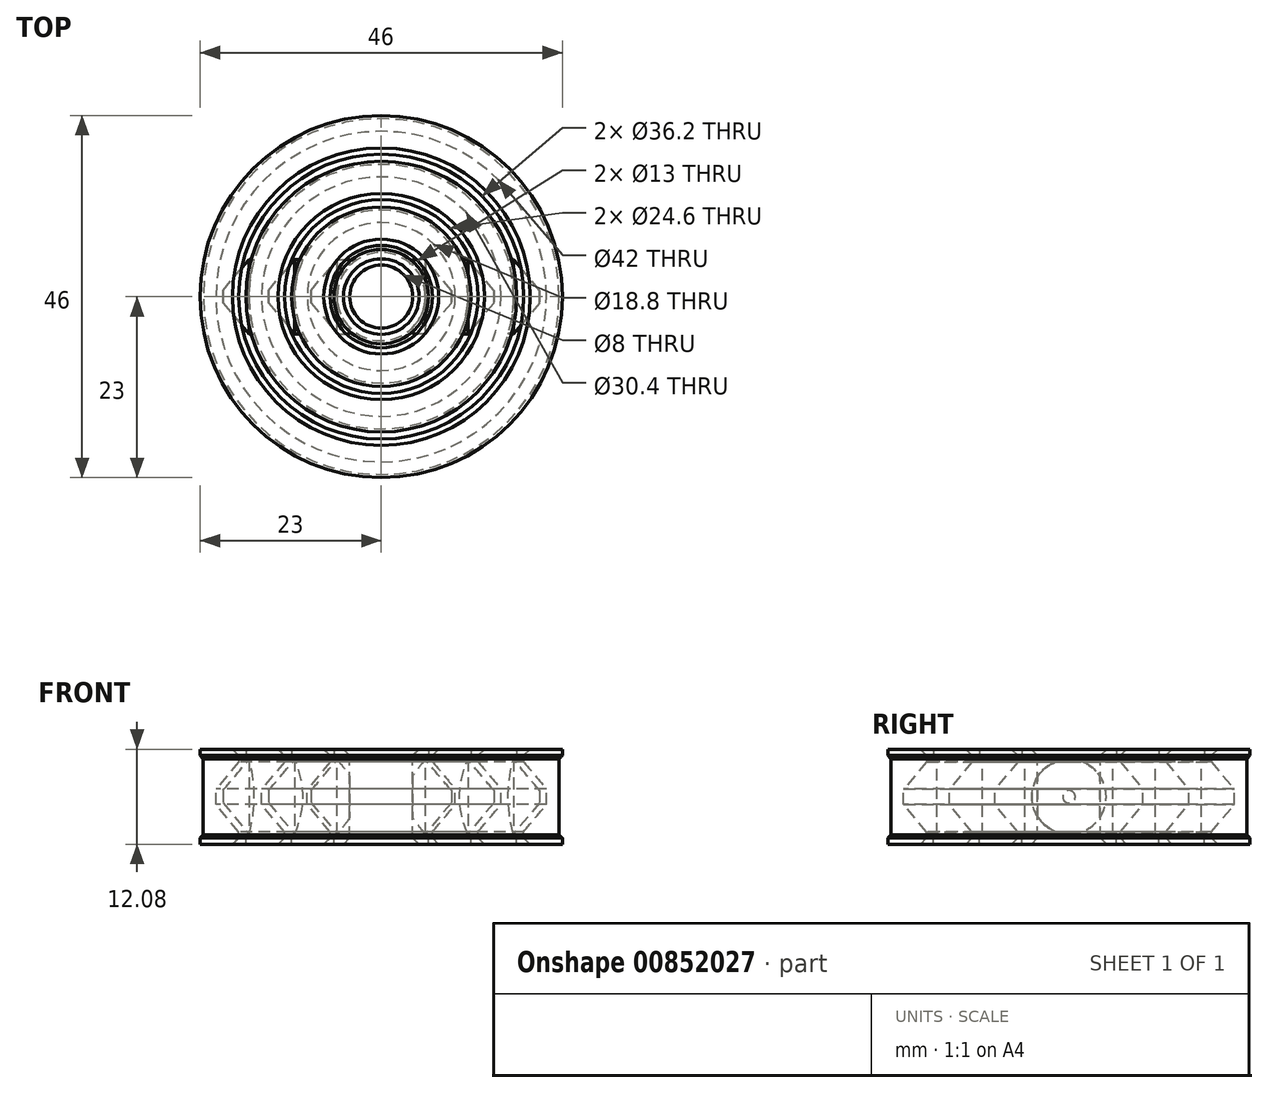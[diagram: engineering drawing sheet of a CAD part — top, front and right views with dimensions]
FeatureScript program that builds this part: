
annotation { "Feature Type Name" : "Feature", "Feature Type Description" : "" }
export const myFeature = defineFeature(function(context is Context, id is Id, definition is map)
    precondition{}
    {
        {
            assignVariable(context, id + "F0", {"name" : "Extrusion", "anyValue" : 0.4});
        }
        {
            assignVariable(context, id + "F1", {"name" : "Shells", "anyValue" : 2});
        }
        {
            assignVariable(context, id + "F2", {"name" : "MinStruct", "anyValue" : getVariable(context, 'Extrusion') * getVariable(context, 'Shells')});
        }
        {
            var Q0;
            Q0=qCreatedBy(makeId("Front.planeOp"),FACE);
            var sketch = newSketch(context, id + "F3", { "sketchPlane" : qUnion([Q0])});
            skLineSegment(sketch, "E0", {"start": v(0, 0) * mm, "end": v(0, -6.04) * mm});
            skLineSegment(sketch, "E1", {"start": v(0, -6.04) * mm, "end": v(5.6, -6.04) * mm});
            skLineSegment(sketch, "E2", {"start": v(5.6, -6.04) * mm, "end": v(5.6, 0) * mm});
            skLineSegment(sketch, "E3", {"start": v(5.6, 0) * mm, "end": v(0, 0) * mm});
            skLineSegment(sketch, "E4", {"start": v(5.6, -4.73) * mm, "end": v(8.9, -0.8) * mm});
            skLineSegment(sketch, "E5", {"start": v(8.9, -0.8) * mm, "end": v(8.9, 0) * mm});
            skLineSegment(sketch, "E6", {"start": v(8.9, 0) * mm, "end": v(5.6, 0) * mm});
            skLineSegment(sketch, "E7", {"start": v(6.5, -6.04) * mm, "end": v(6.5, -4.44) * mm});
            skLineSegment(sketch, "E8", {"start": v(6.5, -4.44) * mm, "end": v(9.4, -0.98) * mm});
            skLineSegment(sketch, "E9", {"start": v(9.4, -0.98) * mm, "end": v(9.4, 0) * mm});
            skLineSegment(sketch, "E10", {"start": v(9.4, 0) * mm, "end": v(11, 0) * mm});
            skLineSegment(sketch, "E11", {"start": v(11, 0) * mm, "end": v(11, -6.04) * mm});
            skLineSegment(sketch, "E12", {"start": v(11, -6.04) * mm, "end": v(6.5, -6.04) * mm});
            skLineSegment(sketch, "E13", {"start": v(4, -6.04) * mm, "end": v(4, 0) * mm});
            skLineSegment(sketch, "E14", {"start": v(11, -4.73) * mm, "end": v(14.3, -0.8) * mm});
            skLineSegment(sketch, "E15", {"start": v(14.3, -0.8) * mm, "end": v(14.3, 0) * mm});
            skLineSegment(sketch, "E16", {"start": v(14.3, 0) * mm, "end": v(11, 0) * mm});
            skArc(sketch, "E17", {"start": v(6.5, -8.87) * mm, "mid": v(9.81, -4.97) * mm, "end": v(11, 0) * mm});
            skPoint(sketch, "E18", {"position": v(6.5, -5.24) * mm});
            skArc(sketch, "E19", {"start": v(4, -3.92) * mm, "mid": v(5.18, -2.12) * mm, "end": v(5.6, 0) * mm});
            skLineSegment(sketch, "E20", {"start": v(5.6, -4.73) * mm, "end": v(4, -4.73) * mm});
            skLineSegment(sketch, "E21", {"start": v(11, -4.73) * mm, "end": v(9.93, -4.73) * mm});
            skLineSegment(sketch, "E22.1.0.0", {"start": v(20.1, 0) * mm, "end": v(16.8, 0) * mm});
            skLineSegment(sketch, "E22.1.0.1", {"start": v(20.1, -0.8) * mm, "end": v(20.1, 0) * mm});
            skLineSegment(sketch, "E22.1.0.2", {"start": v(16.8, -4.73) * mm, "end": v(20.1, -0.8) * mm});
            skLineSegment(sketch, "E22.1.0.3", {"start": v(16.8, 0) * mm, "end": v(16.8, -6.04) * mm});
            skLineSegment(sketch, "E22.1.0.4", {"start": v(16.8, -6.04) * mm, "end": v(12.3, -6.04) * mm});
            skLineSegment(sketch, "E22.1.0.5", {"start": v(12.3, -6.04) * mm, "end": v(12.3, -4.44) * mm});
            skLineSegment(sketch, "E22.1.0.6", {"start": v(12.3, -4.44) * mm, "end": v(15.2, -0.98) * mm});
            skLineSegment(sketch, "E22.1.0.7", {"start": v(15.2, -0.98) * mm, "end": v(15.2, 0) * mm});
            skLineSegment(sketch, "E22.1.0.8", {"start": v(15.2, 0) * mm, "end": v(16.8, 0) * mm});
            skLineSegment(sketch, "E22.2.0.0", {"start": v(25.9, 0) * mm, "end": v(22.6, 0) * mm});
            skLineSegment(sketch, "E22.2.0.1", {"start": v(25.9, -0.8) * mm, "end": v(25.9, 0) * mm});
            skLineSegment(sketch, "E22.2.0.2", {"start": v(22.6, -4.73) * mm, "end": v(25.9, -0.8) * mm});
            skLineSegment(sketch, "E22.2.0.3", {"start": v(22.6, 0) * mm, "end": v(22.6, -6.04) * mm});
            skLineSegment(sketch, "E22.2.0.4", {"start": v(22.6, -6.04) * mm, "end": v(18.1, -6.04) * mm});
            skLineSegment(sketch, "E22.2.0.5", {"start": v(18.1, -6.04) * mm, "end": v(18.1, -4.44) * mm});
            skLineSegment(sketch, "E22.2.0.6", {"start": v(18.1, -4.44) * mm, "end": v(21, -0.98) * mm});
            skLineSegment(sketch, "E22.2.0.7", {"start": v(21, -0.98) * mm, "end": v(21, 0) * mm});
            skLineSegment(sketch, "E22.2.0.8", {"start": v(21, 0) * mm, "end": v(22.6, 0) * mm});
            skLineSegment(sketch, "E22.direction1", {"start": v(6.5, -6.04) * mm, "end": v(12.3, -6.04) * mm, "construction": true});
            skArc(sketch, "E23", {"start": v(15.68, -6.04) * mm, "mid": v(16.52, -3.07) * mm, "end": v(16.8, 0) * mm});
            skArc(sketch, "E24", {"start": v(21.78, -6.04) * mm, "mid": v(22.4, -3.05) * mm, "end": v(22.6, 0) * mm});
            skLineSegment(sketch, "E25", {"start": v(16.8, -4.73) * mm, "end": v(16.12, -4.73) * mm});
            skLineSegment(sketch, "E26", {"start": v(22.6, -4.73) * mm, "end": v(22.1, -4.73) * mm});
            skLineSegment(sketch, "E27", {"start": v(5.6, -6.04) * mm, "end": v(6, -6.04) * mm});
            skLineSegment(sketch, "E28", {"start": v(6, -6.04) * mm, "end": v(6, -5.24) * mm});
            skLineSegment(sketch, "E29", {"start": v(6, -5.24) * mm, "end": v(5.6, -4.84) * mm});
            skLineSegment(sketch, "E30", {"start": v(11, -4.84) * mm, "end": v(11.4, -5.24) * mm});
            skLineSegment(sketch, "E31", {"start": v(11.4, -5.24) * mm, "end": v(11.4, -6.04) * mm});
            skLineSegment(sketch, "E32", {"start": v(11.4, -6.04) * mm, "end": v(11, -6.04) * mm});
            skLineSegment(sketch, "E33", {"start": v(16.8, -4.84) * mm, "end": v(17.2, -5.24) * mm});
            skLineSegment(sketch, "E34", {"start": v(17.2, -5.24) * mm, "end": v(17.2, -6.04) * mm});
            skLineSegment(sketch, "E35", {"start": v(17.2, -6.04) * mm, "end": v(16.8, -6.04) * mm});
            skLineSegment(sketch, "E36", {"start": v(22.6, -4.84) * mm, "end": v(23, -5.24) * mm});
            skLineSegment(sketch, "E37", {"start": v(23, -5.24) * mm, "end": v(23, -6.04) * mm});
            skLineSegment(sketch, "E38", {"start": v(23, -6.04) * mm, "end": v(22.6, -6.04) * mm});
            skSolve(sketch);
        }
        {
            var Q0;
            {var subQ5=sQuery(id+"F3.wireOp",EDGE,"E20");Q0=makeQuery(id+"F3.imprint","IMPRINT",FACE,{"disambiguationData":[TD([[makeQuery(id+"F3.imprint","IMPRINT",EDGE,{"derivedFrom":subQ5}),1.0]])]});}
            var Q1;
            {var subQ0=sQuery(id+"F3.wireOp",EDGE,"E19");Q1=makeQuery(id+"F3.imprint","IMPRINT",FACE,{"disambiguationData":[TD([[makeQuery(id+"F3.imprint","IMPRINT",EDGE,{"derivedFrom":subQ0}),-1.0]])]});}
            var Q2;
            {var subQ0=sQuery(id+"F3.wireOp",EDGE,"E19");Q2=makeQuery(id+"F3.imprint","IMPRINT",FACE,{"disambiguationData":[TD([[makeQuery(id+"F3.imprint","IMPRINT",EDGE,{"derivedFrom":subQ0}),1.0]])]});}
            var Q3;
            {var subQ5=sQuery(id+"F3.wireOp",EDGE,"E7");Q3=makeQuery(id+"F3.imprint","IMPRINT",FACE,{"disambiguationData":[TD([[makeQuery(id+"F3.imprint","IMPRINT",EDGE,{"derivedFrom":subQ5}),-1.0]])]});}
            var Q4;
            {var subQ3=sQuery(id+"F3.wireOp",EDGE,"E21");Q4=makeQuery(id+"F3.imprint","IMPRINT",FACE,{"disambiguationData":[TD([[makeQuery(id+"F3.imprint","IMPRINT",EDGE,{"derivedFrom":subQ3}),1.0]])]});}
            var Q5;
            {var subQ3=sQuery(id+"F3.wireOp",EDGE,"E21");Q5=makeQuery(id+"F3.imprint","IMPRINT",FACE,{"disambiguationData":[TD([[makeQuery(id+"F3.imprint","IMPRINT",EDGE,{"derivedFrom":subQ3}),-1.0]])]});}
            var Q6;
            {var subQ0=sQuery(id+"F3.wireOp",EDGE,"E22.1.0.5");Q6=makeQuery(id+"F3.imprint","IMPRINT",FACE,{"disambiguationData":[TD([[makeQuery(id+"F3.imprint","IMPRINT",EDGE,{"derivedFrom":subQ0}),-1.0]])]});}
            var Q7;
            {var subQ3=sQuery(id+"F3.wireOp",EDGE,"E25");Q7=makeQuery(id+"F3.imprint","IMPRINT",FACE,{"disambiguationData":[TD([[makeQuery(id+"F3.imprint","IMPRINT",EDGE,{"derivedFrom":subQ3}),-1.0]])]});}
            var Q8;
            {var subQ0=sQuery(id+"F3.wireOp",EDGE,"E25");Q8=makeQuery(id+"F3.imprint","IMPRINT",FACE,{"disambiguationData":[TD([[makeQuery(id+"F3.imprint","IMPRINT",EDGE,{"derivedFrom":subQ0}),1.0]])]});}
            var Q9;
            {var subQ0=sQuery(id+"F3.wireOp",EDGE,"E22.2.0.5");Q9=makeQuery(id+"F3.imprint","IMPRINT",FACE,{"disambiguationData":[TD([[makeQuery(id+"F3.imprint","IMPRINT",EDGE,{"derivedFrom":subQ0}),-1.0]])]});}
            var Q10;
            {var subQ3=sQuery(id+"F3.wireOp",EDGE,"E26");Q10=makeQuery(id+"F3.imprint","IMPRINT",FACE,{"disambiguationData":[TD([[makeQuery(id+"F3.imprint","IMPRINT",EDGE,{"derivedFrom":subQ3}),-1.0]])]});}
            var Q11;
            {var subQ0=sQuery(id+"F3.wireOp",EDGE,"E26");Q11=makeQuery(id+"F3.imprint","IMPRINT",FACE,{"disambiguationData":[TD([[makeQuery(id+"F3.imprint","IMPRINT",EDGE,{"derivedFrom":subQ0}),1.0]])]});}
            var Q12;
            {var subQ1=sQuery(id+"F3.wireOp",EDGE,"E3");var subQ3=sQuery(id+"F3.wireOp",EDGE,"E13");var subQ4=makeQuery(id+"F3.imprint","INTERSECT",VERTEX,{"derivedFrom":[subQ1,subQ3]});Q12=makeQuery(id+"F3.imprint","IMPRINT",FACE,{"disambiguationData":[TD([[makeQuery(id+"F3.imprint","IMPRINT",EDGE,{"disambiguationData":[TD([[subQ4,1.0]])],"derivedFrom":subQ3}),-1.0]])]});}
            var Q13;
            {var subQ5=sQuery(id+"F3.wireOp",EDGE,"E1");var subQ7=sQuery(id+"F3.wireOp",EDGE,"E2");var subQ8=makeQuery(id+"F3.imprint","INTERSECT",VERTEX,{"derivedFrom":[subQ5,subQ7]});Q13=makeQuery(id+"F3.imprint","IMPRINT",FACE,{"disambiguationData":[TD([[makeQuery(id+"F3.imprint","IMPRINT",EDGE,{"disambiguationData":[TD([[subQ8,1.0]])],"derivedFrom":subQ5}),1.0]])]});}
            var Q14;
            {var subQ0=sQuery(id+"F3.wireOp",EDGE,"E27");Q14=makeQuery(id+"F3.imprint","IMPRINT",FACE,{"disambiguationData":[TD([[makeQuery(id+"F3.imprint","IMPRINT",EDGE,{"derivedFrom":subQ0}),1.0]])]});}
            var Q15;
            {var subQ2=sQuery(id+"F3.wireOp",EDGE,"E30");Q15=makeQuery(id+"F3.imprint","IMPRINT",FACE,{"disambiguationData":[TD([[makeQuery(id+"F3.imprint","IMPRINT",EDGE,{"derivedFrom":subQ2}),-1.0]])]});}
            var Q16;
            {var subQ2=sQuery(id+"F3.wireOp",EDGE,"E33");Q16=makeQuery(id+"F3.imprint","IMPRINT",FACE,{"disambiguationData":[TD([[makeQuery(id+"F3.imprint","IMPRINT",EDGE,{"derivedFrom":subQ2}),-1.0]])]});}
            var Q17;
            {var subQ2=sQuery(id+"F3.wireOp",EDGE,"E36");Q17=makeQuery(id+"F3.imprint","IMPRINT",FACE,{"disambiguationData":[TD([[makeQuery(id+"F3.imprint","IMPRINT",EDGE,{"derivedFrom":subQ2}),-1.0]])]});}
            var Q18;
            Q18=sQuery(id+"F3.wireOp",EDGE,"E0");
            revolve(context, id + "F4", {"surfaceOperationType" : NewSurfaceOperationType.NEW, "entities" : qUnion([Q0, Q1, Q2, Q3, Q4, Q5, Q6, Q7, Q8, Q9, Q10, Q11, Q12, Q13, Q14, Q15, Q16, Q17]), "axis" : qUnion([Q18]), "revolveType" : RevolveType.SYMMETRIC, "angle" : 180 * degree});
        }
        {
            var Q0;
            {var subQ2=sQuery(id+"F3.wireOp",EDGE,"E4");Q0=makeQuery(id+"F3.imprint","IMPRINT",FACE,{"disambiguationData":[TD([[makeQuery(id+"F3.imprint","IMPRINT",EDGE,{"derivedFrom":subQ2}),1.0]])]});}
            var Q1;
            {var subQ0=sQuery(id+"F3.wireOp",EDGE,"E19");Q1=makeQuery(id+"F3.imprint","IMPRINT",FACE,{"disambiguationData":[TD([[makeQuery(id+"F3.imprint","IMPRINT",EDGE,{"derivedFrom":subQ0}),-1.0]])]});}
            var Q2;
            {var subQ2=sQuery(id+"F3.wireOp",EDGE,"E14");Q2=makeQuery(id+"F3.imprint","IMPRINT",FACE,{"disambiguationData":[TD([[makeQuery(id+"F3.imprint","IMPRINT",EDGE,{"derivedFrom":subQ2}),1.0]])]});}
            var Q3;
            {var subQ3=sQuery(id+"F3.wireOp",EDGE,"E21");Q3=makeQuery(id+"F3.imprint","IMPRINT",FACE,{"disambiguationData":[TD([[makeQuery(id+"F3.imprint","IMPRINT",EDGE,{"derivedFrom":subQ3}),-1.0]])]});}
            var Q4;
            {var subQ0=sQuery(id+"F3.wireOp",EDGE,"E22.1.0.0");Q4=makeQuery(id+"F3.imprint","IMPRINT",FACE,{"disambiguationData":[TD([[makeQuery(id+"F3.imprint","IMPRINT",EDGE,{"derivedFrom":subQ0}),1.0]])]});}
            var Q5;
            {var subQ3=sQuery(id+"F3.wireOp",EDGE,"E25");Q5=makeQuery(id+"F3.imprint","IMPRINT",FACE,{"disambiguationData":[TD([[makeQuery(id+"F3.imprint","IMPRINT",EDGE,{"derivedFrom":subQ3}),-1.0]])]});}
            var Q6;
            Q6=sQuery(id+"F3.wireOp",EDGE,"E10");
            revolve(context, id + "F5", {"operationType" : NewBodyOperationType.ADD, "surfaceOperationType" : NewSurfaceOperationType.NEW, "entities" : qUnion([Q0, Q1, Q2, Q3, Q4, Q5]), "axis" : qUnion([Q6]), "revolveType" : RevolveType.SYMMETRIC, "angle" : 180 * degree});
        }
        {
            var Q0;
            Q0=makeQuery(id+"F4.opRevolve","SWEPT_EDGE",EDGE,{"disambiguationData":[OSD([sQuery(id+"F3.wireOp",EDGE,"E7"),sQuery(id+"F3.wireOp",EDGE,"E12")])]});
            var Q1;
            Q1=makeQuery(id+"F4.opRevolve","SWEPT_EDGE",EDGE,{"disambiguationData":[OSD([sQuery(id+"F3.wireOp",EDGE,"E22.1.0.4"),sQuery(id+"F3.wireOp",EDGE,"E22.1.0.5")])]});
            var Q2;
            Q2=makeQuery(id+"F4.opRevolve","SWEPT_EDGE",EDGE,{"disambiguationData":[OSD([sQuery(id+"F3.wireOp",EDGE,"E22.2.0.4"),sQuery(id+"F3.wireOp",EDGE,"E22.2.0.5")])]});
            var Q3;
            Q3=makeQuery(id+"F4.opRevolve","SWEPT_EDGE",EDGE,{"disambiguationData":[OSD([sQuery(id+"F3.wireOp",EDGE,"E1"),sQuery(id+"F3.wireOp",EDGE,"E13")])]});
            chamfer(context, id + "F6", {"entities" : qUnion([Q0, Q1, Q2, Q3]), "width" : (getVariable(context, 'MinStruct')) * mm, "tangentPropagation" : true});
        }
        {
            var Q0;
            Q0=makeQuery(id+"F4.opRevolve","SWEPT_BODY",BODY,{"disambiguationData":[OSD([sQuery(id+"F3.wireOp",EDGE,"E1"),sQuery(id+"F3.wireOp",EDGE,"E2"),sQuery(id+"F3.wireOp",EDGE,"E3"),sQuery(id+"F3.wireOp",EDGE,"E13")])]});
            var Q1;
            Q1=makeQuery(id+"F4.opRevolve","SWEPT_BODY",BODY,{"disambiguationData":[OSD([sQuery(id+"F3.wireOp",EDGE,"E7"),sQuery(id+"F3.wireOp",EDGE,"E8"),sQuery(id+"F3.wireOp",EDGE,"E9"),sQuery(id+"F3.wireOp",EDGE,"E10"),sQuery(id+"F3.wireOp",EDGE,"E11"),sQuery(id+"F3.wireOp",EDGE,"E12")])]});
            var Q2;
            Q2=makeQuery(id+"F4.opRevolve","SWEPT_BODY",BODY,{"disambiguationData":[OSD([sQuery(id+"F3.wireOp",EDGE,"E22.1.0.3"),sQuery(id+"F3.wireOp",EDGE,"E22.1.0.4"),sQuery(id+"F3.wireOp",EDGE,"E22.1.0.5"),sQuery(id+"F3.wireOp",EDGE,"E22.1.0.6"),sQuery(id+"F3.wireOp",EDGE,"E22.1.0.7"),sQuery(id+"F3.wireOp",EDGE,"E22.1.0.8")])]});
            var Q3;
            Q3=makeQuery(id+"F4.opRevolve","SWEPT_BODY",BODY,{"disambiguationData":[OSD([sQuery(id+"F3.wireOp",EDGE,"E22.2.0.3"),sQuery(id+"F3.wireOp",EDGE,"E22.2.0.4"),sQuery(id+"F3.wireOp",EDGE,"E22.2.0.5"),sQuery(id+"F3.wireOp",EDGE,"E22.2.0.6"),sQuery(id+"F3.wireOp",EDGE,"E22.2.0.7"),sQuery(id+"F3.wireOp",EDGE,"E22.2.0.8")])]});
            var Q4;
            Q4=makeQuery(id+"F5.boolean.opBoolean","MERGE",FACE,{"derivedFrom":[makeQuery(id+"F4.opRevolve","SWEPT_FACE",FACE,{"disambiguationData":[OSD([sQuery(id+"F3.wireOp",EDGE,"E3")])]}),makeQuery(id+"F5.opRevolve","CAP_FACE",FACE,{"disambiguationData":[OSD([sQuery(id+"F3.wireOp",EDGE,"E4"),sQuery(id+"F3.wireOp",EDGE,"E5"),sQuery(id+"F3.wireOp",EDGE,"E6"),sQuery(id+"F3.wireOp",EDGE,"E19"),sQuery(id+"F3.wireOp",EDGE,"E20")])],"isStart":true})]});
            mirror(context, id + "F7", {"operationType" : NewBodyOperationType.ADD, "entities" : qUnion([Q0, Q1, Q2, Q3]), "mirrorPlane" : qUnion([Q4])});
        }
        {
            var Q0;
            Q0=makeQuery(id+"F4.opRevolve","SWEPT_BODY",BODY,{"disambiguationData":[OSD([sQuery(id+"F3.wireOp",EDGE,"E22.2.0.3"),sQuery(id+"F3.wireOp",EDGE,"E22.2.0.4"),sQuery(id+"F3.wireOp",EDGE,"E22.2.0.5"),sQuery(id+"F3.wireOp",EDGE,"E22.2.0.6"),sQuery(id+"F3.wireOp",EDGE,"E22.2.0.7"),sQuery(id+"F3.wireOp",EDGE,"E22.2.0.8")])]});
            var Q1;
            Q1=makeQuery(id+"F4.opRevolve","SWEPT_BODY",BODY,{"disambiguationData":[OSD([sQuery(id+"F3.wireOp",EDGE,"E22.1.0.3"),sQuery(id+"F3.wireOp",EDGE,"E22.1.0.4"),sQuery(id+"F3.wireOp",EDGE,"E22.1.0.5"),sQuery(id+"F3.wireOp",EDGE,"E22.1.0.6"),sQuery(id+"F3.wireOp",EDGE,"E22.1.0.7"),sQuery(id+"F3.wireOp",EDGE,"E22.1.0.8")])]});
            var Q2;
            Q2=makeQuery(id+"F4.opRevolve","SWEPT_BODY",BODY,{"disambiguationData":[OSD([sQuery(id+"F3.wireOp",EDGE,"E7"),sQuery(id+"F3.wireOp",EDGE,"E8"),sQuery(id+"F3.wireOp",EDGE,"E9"),sQuery(id+"F3.wireOp",EDGE,"E10"),sQuery(id+"F3.wireOp",EDGE,"E11"),sQuery(id+"F3.wireOp",EDGE,"E12")])]});
            var Q3;
            Q3=makeQuery(id+"F4.opRevolve","SWEPT_BODY",BODY,{"disambiguationData":[OSD([sQuery(id+"F3.wireOp",EDGE,"E1"),sQuery(id+"F3.wireOp",EDGE,"E2"),sQuery(id+"F3.wireOp",EDGE,"E3"),sQuery(id+"F3.wireOp",EDGE,"E13")])]});
            var Q4;
            {var subQ0=makeQuery(id+"F4.opRevolve","CAP_FACE",FACE,{"disambiguationData":[OSD([sQuery(id+"F3.wireOp",EDGE,"E1"),sQuery(id+"F3.wireOp",EDGE,"E2"),sQuery(id+"F3.wireOp",EDGE,"E3"),sQuery(id+"F3.wireOp",EDGE,"E13")])],"isStart":true});Q4=makeQuery(id+"F7.boolean.opBoolean","MERGE",FACE,{"derivedFrom":[subQ0,makeQuery(id+"F7.opPattern","COPY",FACE,{"derivedFrom":subQ0,"instanceName":"1"})]});}
            mirror(context, id + "F8", {"operationType" : NewBodyOperationType.ADD, "entities" : qUnion([Q0, Q1, Q2, Q3]), "mirrorPlane" : qUnion([Q4])});
        }
    });
